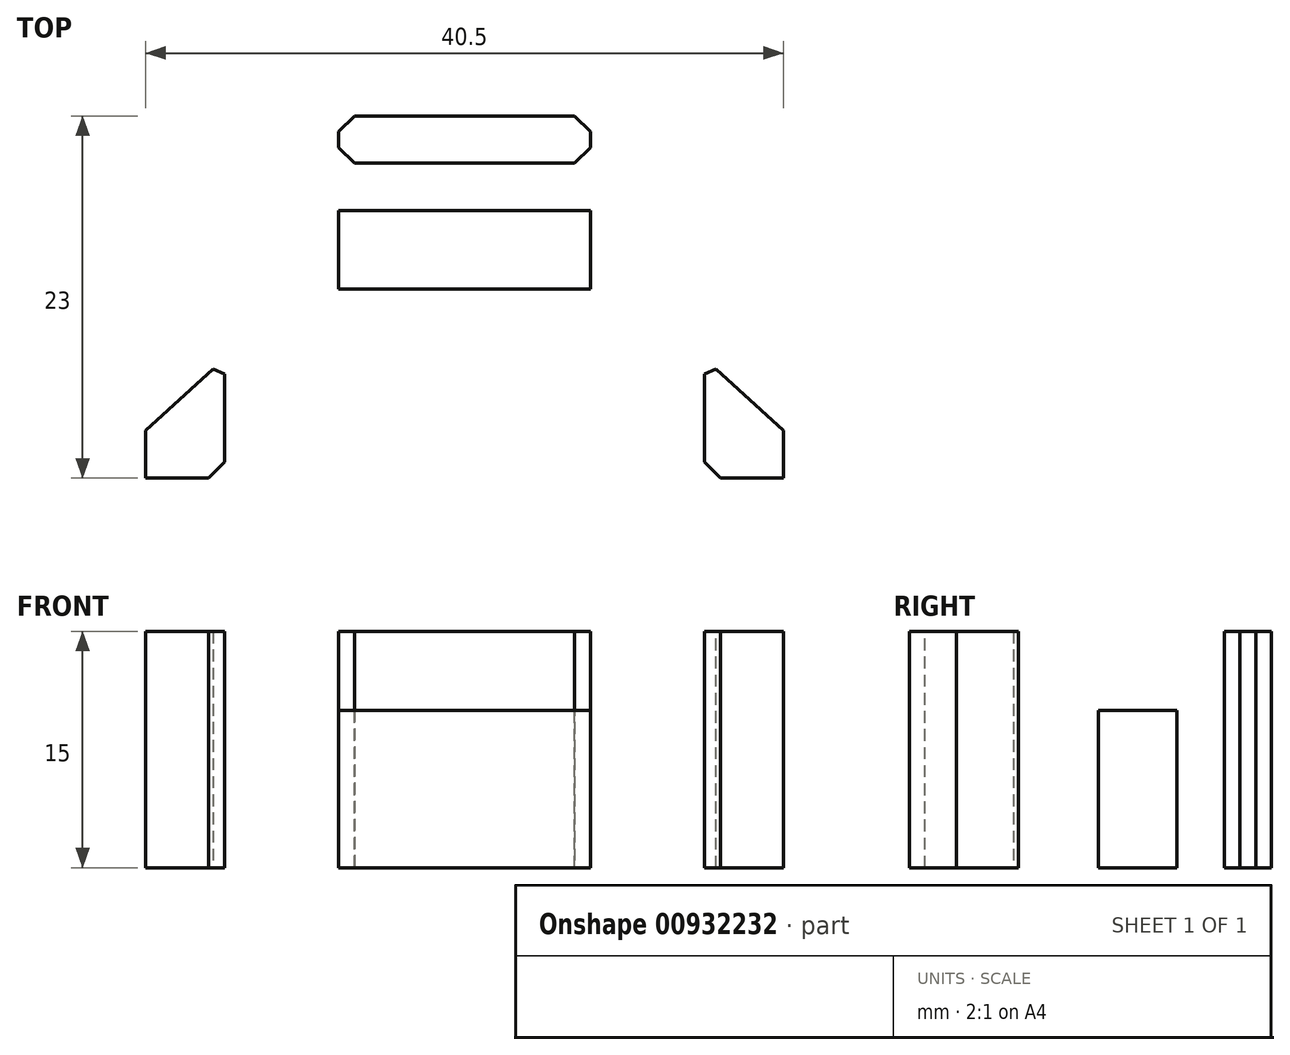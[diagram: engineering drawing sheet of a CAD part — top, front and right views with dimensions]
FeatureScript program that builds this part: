
annotation { "Feature Type Name" : "Feature", "Feature Type Description" : "" }
export const myFeature = defineFeature(function(context is Context, id is Id, definition is map)
    precondition{}
    {
        {
            var Q0;
            Q0=qCreatedBy(makeId("Top.planeOp"),FACE);
            var sketch = newSketch(context, id + "F0", { "sketchPlane" : qUnion([Q0])});
            skLineSegment(sketch, "E0.left", {"start": v(-15.25, 0) * mm, "end": v(-15.25, 26) * mm});
            skLineSegment(sketch, "E0.right", {"start": v(15.25, 0) * mm, "end": v(15.25, 26) * mm});
            skLineSegment(sketch, "E1.top", {"start": v(-13.25, 23) * mm, "end": v(13.25, 23) * mm});
            skLineSegment(sketch, "E1.left", {"start": v(-13.25, 0) * mm, "end": v(-13.25, 23) * mm});
            skLineSegment(sketch, "E1.right", {"start": v(13.25, 0) * mm, "end": v(13.25, 23) * mm});
            skLineSegment(sketch, "E2", {"start": v(-15.25, 0) * mm, "end": v(-13.25, 0) * mm});
            skLineSegment(sketch, "E3", {"start": v(13.25, 0) * mm, "end": v(15.25, 0) * mm});
            skLineSegment(sketch, "E4.bottom", {"start": v(-8, 23) * mm, "end": v(8, 23) * mm});
            skLineSegment(sketch, "E4.top", {"start": v(-8, 20) * mm, "end": v(8, 20) * mm});
            skLineSegment(sketch, "E4.left", {"start": v(-8, 23) * mm, "end": v(-8, 20) * mm});
            skLineSegment(sketch, "E4.right", {"start": v(8, 23) * mm, "end": v(8, 20) * mm});
            skLineSegment(sketch, "E5.top", {"start": v(-5, 25) * mm, "end": v(5, 25) * mm});
            skLineSegment(sketch, "E5.left", {"start": v(-5, 26) * mm, "end": v(-5, 25) * mm});
            skLineSegment(sketch, "E5.right", {"start": v(5, 26) * mm, "end": v(5, 25) * mm});
            skLineSegment(sketch, "E6", {"start": v(-15.25, 26) * mm, "end": v(-5, 26) * mm});
            skLineSegment(sketch, "E7", {"start": v(5, 26) * mm, "end": v(15.25, 26) * mm});
            skLineSegment(sketch, "E8", {"start": v(15.25, 0) * mm, "end": v(20.25, 0) * mm});
            skLineSegment(sketch, "E9", {"start": v(20.25, 0) * mm, "end": v(20.25, 3) * mm});
            skLineSegment(sketch, "E10", {"start": v(20.25, 3) * mm, "end": v(15.25, 7.61) * mm});
            skLineSegment(sketch, "E11", {"start": v(-15.25, 0) * mm, "end": v(-20.25, 0) * mm});
            skLineSegment(sketch, "E12", {"start": v(-20.25, 0) * mm, "end": v(-20.25, 3) * mm});
            skLineSegment(sketch, "E13", {"start": v(-20.25, 3) * mm, "end": v(-15.25, 7.61) * mm});
            skLineSegment(sketch, "E14.bottom", {"start": v(-8, 17) * mm, "end": v(8, 17) * mm});
            skLineSegment(sketch, "E14.top", {"start": v(-8, 12) * mm, "end": v(8, 12) * mm});
            skLineSegment(sketch, "E14.left", {"start": v(-8, 17) * mm, "end": v(-8, 12) * mm});
            skLineSegment(sketch, "E14.right", {"start": v(8, 17) * mm, "end": v(8, 12) * mm});
            skSolve(sketch);
        }
        {
            var Q0;
            {var subQ2=sQuery(id+"F0.wireOp",EDGE,"E1.left");Q0=makeQuery(id+"F0.imprint","IMPRINT",FACE,{"disambiguationData":[TD([[makeQuery(id+"F0.imprint","IMPRINT",EDGE,{"derivedFrom":subQ2}),1.0]])]});}
            var Q1;
            Q1=makeQuery(id+"F0.imprint","IMPRINT",FACE,{"disambiguationData":[TD([[makeQuery(id+"F0.imprint","IMPRINT",EDGE,{"derivedFrom":sQuery(id+"F0.wireOp",EDGE,"E4.top")}),1.0]])]});
            var Q2;
            {var subQ2=sQuery(id+"F0.wireOp",EDGE,"E8");Q2=makeQuery(id+"F0.imprint","IMPRINT",FACE,{"disambiguationData":[TD([[makeQuery(id+"F0.imprint","IMPRINT",EDGE,{"derivedFrom":subQ2}),1.0]])]});}
            var Q3;
            {var subQ2=sQuery(id+"F0.wireOp",EDGE,"E11");Q3=makeQuery(id+"F0.imprint","IMPRINT",FACE,{"disambiguationData":[TD([[makeQuery(id+"F0.imprint","IMPRINT",EDGE,{"derivedFrom":subQ2}),-1.0]])]});}
            extrude(context, id + "F1", {"entities" : qUnion([Q0, Q1, Q2, Q3]), "depth" : 15 * mm, "offsetDistance" : 25 * mm});
        }
        {
            var Q0;
            Q0=makeQuery(id+"F1.opExtrude","SWEPT_EDGE",EDGE,{"disambiguationData":[OSD([sQuery(id+"F0.wireOp",EDGE,"E1.top"),sQuery(id+"F0.wireOp",EDGE,"E1.left")])]});
            var Q1;
            Q1=makeQuery(id+"F1.opExtrude","SWEPT_EDGE",EDGE,{"disambiguationData":[OSD([sQuery(id+"F0.wireOp",EDGE,"E1.top"),sQuery(id+"F0.wireOp",EDGE,"E1.right")])]});
            var Q2;
            Q2=makeQuery(id+"F1.opExtrude","SWEPT_EDGE",EDGE,{"disambiguationData":[OSD([sQuery(id+"F0.wireOp",EDGE,"E0.right"),sQuery(id+"F0.wireOp",EDGE,"E7")])]});
            var Q3;
            Q3=makeQuery(id+"F1.opExtrude","SWEPT_EDGE",EDGE,{"disambiguationData":[OSD([sQuery(id+"F0.wireOp",EDGE,"E0.left"),sQuery(id+"F0.wireOp",EDGE,"E6")])]});
            var Q4;
            Q4=makeQuery(id+"F1.opExtrude","SWEPT_EDGE",EDGE,{"disambiguationData":[OSD([sQuery(id+"F0.wireOp",EDGE,"E5.left"),sQuery(id+"F0.wireOp",EDGE,"E6")])]});
            var Q5;
            Q5=makeQuery(id+"F1.opExtrude","SWEPT_EDGE",EDGE,{"disambiguationData":[OSD([sQuery(id+"F0.wireOp",EDGE,"E5.right"),sQuery(id+"F0.wireOp",EDGE,"E7")])]});
            var Q6;
            Q6=makeQuery(id+"F1.opExtrude","SWEPT_EDGE",EDGE,{"disambiguationData":[OSD([sQuery(id+"F0.wireOp",EDGE,"E1.top"),sQuery(id+"F0.wireOp",EDGE,"E4.left")])]});
            var Q7;
            Q7=makeQuery(id+"F1.opExtrude","SWEPT_EDGE",EDGE,{"disambiguationData":[OSD([sQuery(id+"F0.wireOp",EDGE,"E4.top"),sQuery(id+"F0.wireOp",EDGE,"E4.left")])]});
            var Q8;
            Q8=makeQuery(id+"F1.opExtrude","SWEPT_EDGE",EDGE,{"disambiguationData":[OSD([sQuery(id+"F0.wireOp",EDGE,"E1.top"),sQuery(id+"F0.wireOp",EDGE,"E4.right")])]});
            var Q9;
            Q9=makeQuery(id+"F1.opExtrude","SWEPT_EDGE",EDGE,{"disambiguationData":[OSD([sQuery(id+"F0.wireOp",EDGE,"E4.top"),sQuery(id+"F0.wireOp",EDGE,"E4.right")])]});
            var Q10;
            Q10=makeQuery(id+"F1.opExtrude","SWEPT_EDGE",EDGE,{"disambiguationData":[OSD([sQuery(id+"F0.wireOp",EDGE,"E1.right"),sQuery(id+"F0.wireOp",EDGE,"E3")])]});
            var Q11;
            Q11=makeQuery(id+"F1.opExtrude","SWEPT_EDGE",EDGE,{"disambiguationData":[OSD([sQuery(id+"F0.wireOp",EDGE,"E1.left"),sQuery(id+"F0.wireOp",EDGE,"E2")])]});
            chamfer(context, id + "F2", {"entities" : qUnion([Q0, Q1, Q2, Q3, Q4, Q5, Q6, Q7, Q8, Q9, Q10, Q11]), "width" : 1 * mm, "tangentPropagation" : true});
        }
        {
            var Q0;
            Q0=makeQuery(id+"F0.imprint","IMPRINT",FACE,{"disambiguationData":[TD([[makeQuery(id+"F0.imprint","IMPRINT",EDGE,{"derivedFrom":sQuery(id+"F0.wireOp",EDGE,"E14.bottom")}),-1.0]])]});
            extrude(context, id + "F3", {"entities" : qUnion([Q0]), "depth" : 10 * mm, "offsetDistance" : 25 * mm});
        }
    });
